# Revit family: Mixer_Basin_Nero_Dolce
name_source: partatom
category: Plumbing Fixtures
units: mm (PartAtom-declared; Revit-internal decimal feet)

## family parameters
Always vertical = Yes
Cut with Voids When Loaded = Yes
Maintain Annotation Orientation = No
OmniClass Number = 23.31.11.19
OmniClass Title = Faucet Mixing Valves
Part Type = Normal
Room Calculation Point = No
Round Connector Dimension = Use Diameter
Shared = No
Work Plane-Based = No

## types (3) — shared parameters
Assembly Code = C1030210
CW Connection = Yes
Description = Dolce Basin Mixer Stylish Spout
HW Connection = Yes
IfcExportAs = ifcValve
IfcExportType = FAUCET
Manufacturer = Nero
ManufacturerOverallDepth = 145 mm
ManufacturerOverallHeight = 156 mm
ManufacturerOverallWidth = 52 mm
ManufacturerURLProductSpecific = https://nerotapware.com.au
ModifiedIssue = 20240428 $
URL = https://nerotapware.com.au
Uniclass2015Code = Pr_40_20_87_55
Uniclass2015Title = Mixer taps
Uniclass2015Version = Products v1.28
Vent Connection = No
Waste Connection = No
zero-valued in all types: Default Elevation

## per-type parameters (varying)
| type | BodyMaterial | ManufacturerSpecCode | Model | Type Comments |
| Brushed Nickel (NR250802aBN) | Metal_Nickel_Nero_Brushed | NR250802aBN | NR250802aBN | Mixer - Basin - Brushed Nickel |
| Matte Black (NR250802aMB) | Metal_MatteBlack_Nero | NR250802aMB | NR250802aMB | Mixer - Basin - Matte Black |
| Chrome (NR250802aCH) | Metal_Chrome_Nero | NR250802aCH | NR250802aCH | Mixer - Basin - Chrome |

## geometry (parser evidence)
native form markers: Sweep x2
no freeform markers — native parametric forms only
